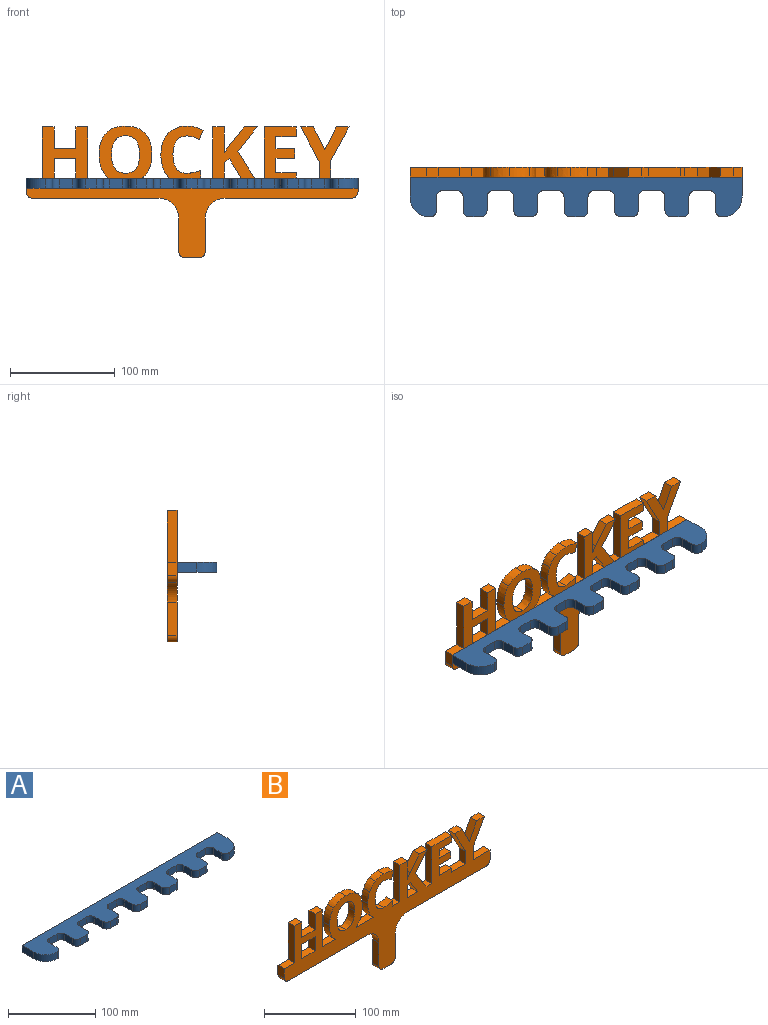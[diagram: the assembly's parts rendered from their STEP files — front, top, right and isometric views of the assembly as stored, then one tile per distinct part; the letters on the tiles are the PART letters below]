
ASSEMBLY  parts=2 mates=1
PART A: 54 faces, bbox 317.5x38.1x9.5 mm
  f0: cylinder r=6.35mm len=9.53mm, axis (0,0,-1), area 95mm2, adj f1,f51,f52,f53
  f1: plane 12.7x9.53mm, normal (0,-1,0), area 121mm2, adj f0,f2,f52,f53
  f2: cylinder r=6.35mm len=9.53mm, axis (0,0,-1), area 95mm2, adj f1,f3,f52,f53
  f3: plane 12.7x9.53mm, normal (-1,0,0), area 121mm2, adj f2,f4,f52,f53
  f4: cylinder r=6.35mm len=9.53mm, axis (0,0,-1), area 95mm2, adj f3,f5,f52,f53
  f5: plane 10.16x9.53mm, normal (0,-1,0), area 96.8mm2, adj f4,f6,f52,f53
  f6: cylinder r=6.35mm len=9.53mm, axis (0,0,-1), area 95mm2, adj f5,f7,f52,f53
  f7: plane 12.7x9.53mm, normal (1,0,0), area 121mm2, adj f6,f8,f52,f53
  f8: cylinder r=6.35mm len=9.53mm, axis (0,0,-1), area 95mm2, adj f7,f9,f52,f53
  f9: plane 12.7x9.53mm, normal (0,-1,0), area 121mm2, adj f8,f10,f52,f53
  f10: cylinder r=6.35mm len=9.53mm, axis (0,0,-1), area 95mm2, adj f9,f11,f52,f53
  f11: plane 12.7x9.53mm, normal (-1,0,0), area 121mm2, adj f10,f12,f52,f53
  f12: cylinder r=6.35mm len=9.53mm, axis (0,0,-1), area 95mm2, adj f11,f13,f52,f53
  f13: plane 10.16x9.53mm, normal (0,-1,0), area 96.8mm2, adj f12,f14,f52,f53
  f14: cylinder r=6.35mm len=9.53mm, axis (0,0,-1), area 95mm2, adj f13,f15,f52,f53
  f15: plane 12.7x9.53mm, normal (1,0,0), area 121mm2, adj f14,f16,f52,f53
  f16: cylinder r=6.35mm len=9.53mm, axis (0,0,-1), area 95mm2, adj f15,f17,f52,f53
  f17: plane 12.7x9.53mm, normal (0,-1,0), area 121mm2, adj f16,f18,f52,f53
  f18: cylinder r=6.35mm len=9.53mm, axis (0,0,-1), area 95mm2, adj f17,f19,f52,f53
  f19: plane 12.7x9.53mm, normal (-1,0,0), area 121mm2, adj f18,f20,f52,f53
  f20: cylinder r=6.35mm len=9.53mm, axis (0,0,-1), area 95mm2, adj f19,f21,f52,f53
  f21: plane 10.16x9.53mm, normal (0,-1,0), area 96.8mm2, adj f20,f22,f52,f53
  f22: cylinder r=6.35mm len=9.53mm, axis (0,0,-1), area 95mm2, adj f21,f23,f52,f53
  f23: plane 12.7x9.53mm, normal (1,0,0), area 121mm2, adj f22,f24,f52,f53
  f24: cylinder r=6.35mm len=9.53mm, axis (0,0,-1), area 95mm2, adj f23,f25,f52,f53
  f25: plane 12.7x9.53mm, normal (0,-1,0), area 121mm2, adj f24,f26,f52,f53
  f26: cylinder r=6.35mm len=9.53mm, axis (0,0,-1), area 95mm2, adj f25,f27,f52,f53
  f27: plane 12.7x9.53mm, normal (-1,0,0), area 121mm2, adj f26,f28,f52,f53
  f28: cylinder r=6.35mm len=9.53mm, axis (0,0,-1), area 95mm2, adj f27,f29,f52,f53
  f29: plane 10.16x9.53mm, normal (0,-1,0), area 96.8mm2, adj f28,f30,f52,f53
  f30: cylinder r=6.35mm len=9.53mm, axis (0,0,-1), area 95mm2, adj f29,f31,f52,f53
  f31: plane 12.7x9.53mm, normal (1,0,0), area 121mm2, adj f30,f32,f52,f53
  f32: cylinder r=6.35mm len=9.53mm, axis (0,0,-1), area 95mm2, adj f31,f33,f52,f53
  f33: plane 12.7x9.53mm, normal (0,-1,0), area 121mm2, adj f32,f34,f52,f53
  f34: cylinder r=6.35mm len=9.53mm, axis (0,0,-1), area 95mm2, adj f33,f35,f52,f53
  f35: plane 12.7x9.53mm, normal (-1,0,0), area 121mm2, adj f34,f36,f52,f53
  f36: cylinder r=6.35mm len=9.53mm, axis (0,0,-1), area 95mm2, adj f35,f37,f52,f53
  f37: plane 10.16x9.53mm, normal (0,-1,0), area 96.8mm2, adj f36,f38,f52,f53
  f38: cylinder r=6.35mm len=9.53mm, axis (0,0,-1), area 95mm2, adj f37,f39,f52,f53
  f39: plane 12.7x9.53mm, normal (1,0,0), area 121mm2, adj f38,f40,f52,f53
  f40: cylinder r=6.35mm len=9.53mm, axis (0,0,-1), area 95mm2, adj f39,f41,f52,f53
  f41: plane 12.7x9.53mm, normal (0,-1,0), area 121mm2, adj f40,f42,f52,f53
  f42: cylinder r=6.35mm len=9.53mm, axis (0,0,-1), area 95mm2, adj f41,f43,f52,f53
  f43: plane 12.7x9.53mm, normal (-1,0,0), area 121mm2, adj f42,f44,f52,f53
  f44: cylinder r=6.35mm len=9.53mm, axis (0,0,-1), area 95mm2, adj f43,f45,f52,f53
  f45: cylinder r=19.05mm len=19.05mm, axis (0,0,-1), area 285mm2, adj f44,f46,f52,f53
  f46: plane 19.05x9.53mm, normal (1,0,0), area 181.5mm2, adj f45,f47,f52,f53
  f47: plane 317.5x9.53mm, normal (0,1,0), area 3024.2mm2, adj f46,f48,f52,f53
  f48: plane 19.05x9.53mm, normal (-1,0,0), area 181.5mm2, adj f47,f49,f52,f53
  f49: cylinder r=19.05mm len=19.05mm, axis (0,0,-1), area 285mm2, adj f48,f50,f52,f53
  f50: cylinder r=6.35mm len=9.53mm, axis (0,0,-1), area 95mm2, adj f49,f51,f52,f53
  f51: plane 12.7x9.53mm, normal (1,0,0), area 121mm2, adj f0,f50,f52,f53
  f52: plane 317.5x38.1mm, normal (0,0,1), area 8070mm2, adj f0,f1,f2,f3,f4,f5,f6,f7
  f53: plane 317.5x38.1mm, normal (0,0,-1), area 8070mm2, adj f0,f1,f2,f3,f4,f5,f6,f7
PART B: 92 faces, bbox 317.5x9.5x126.2 mm
  f0: plane 20.96x9.53mm, normal (0,0,1), area 199.6mm2, adj f1,f89,f90,f91
  f1: plane 19.03x9.53mm, normal (1,0,0), area 181.3mm2, adj f0,f2,f90,f91
  f2: plane 20.96x9.53mm, normal (0,0,-1), area 199.6mm2, adj f1,f89,f90,f91
  f3: plane 18.49x11.5mm, normal (-0.85,0,-0.53), area 207.4mm2, adj f4,f86,f90,f91
  f4: plane 16.24x9.53mm, normal (0,0,1), area 154.6mm2, adj f3,f5,f90,f91
  f5: plane 15.08x9.53mm, normal (1,0,0), area 143.7mm2, adj f4,f86,f90,f91
  f6: extruded ~13.36x9.53mm, area 133.5mm2, adj f7,f87,f90,f91
  f7: extruded ~13.37x9.53mm, area 133.6mm2, adj f6,f8,f90,f91
  f8: extruded ~10.1x9.53mm, area 109.5mm2, adj f7,f9,f90,f91
  f9: extruded ~17.87x13.36mm, area 242.4mm2, adj f8,f10,f90,f91
  f10: extruded ~17.85x13.43mm, area 242.7mm2, adj f9,f87,f90,f91
  f11: plane 49.12x9.53mm, normal (-1,0,0), area 467.8mm2, adj f12,f88,f90,f91
  f12: plane 9.53x9.06mm, normal (0,0,1), area 86.3mm2, adj f11,f13,f90,f91
  f13: plane 25.69x16.2mm, normal (0.85,0,0.53), area 289.3mm2, adj f12,f14,f90,f91
  f14: plane 23.42x18.47mm, normal (0.79,0,-0.62), area 284.1mm2, adj f13,f15,f90,f91
  f15: plane 12.45x9.53mm, normal (0,0,1), area 118.6mm2, adj f14,f16,f90,f91
  f16: plane 17.99x14.34mm, normal (-0.78,0,0.62), area 219.1mm2, adj f15,f17,f90,f91
  f17: plane 9.53x6.23mm, normal (-0.82,0,0.58), area 72.7mm2, adj f16,f18,f90,f91
  f18: plane 24.22x9.53mm, normal (1,0,0), area 230.7mm2, adj f17,f19,f90,f91
  f19: plane 11.23x9.53mm, normal (0,0,1), area 106.9mm2, adj f18,f20,f90,f91
  f20: plane 49.12x9.53mm, normal (-1,0,0), area 467.8mm2, adj f19,f21,f90,f91
  f21: plane 11.26x9.53mm, normal (0,0,1), area 107.2mm2, adj f20,f22,f90,f91
  f22: plane 9.53x7.59mm, normal (1,0,0), area 72.3mm2, adj f21,f23,f90,f91
  f23: extruded ~13.5x9.53mm, area 131.8mm2, adj f22,f24,f90,f91
  f24: extruded ~17.7x13.29mm, area 240.5mm2, adj f23,f25,f90,f91
  f25: extruded ~13.26x9.53mm, area 132.8mm2, adj f24,f26,f90,f91
  f26: extruded ~9.81x9.53mm, area 108.2mm2, adj f25,f27,f90,f91
  f27: extruded ~9.53x5.9mm, area 57.3mm2, adj f26,f28,f90,f91
  f28: extruded ~9.53x5.98mm, area 61.6mm2, adj f27,f29,f90,f91
  f29: plane 9.53x9.13mm, normal (0.93,0,-0.37), area 93.5mm2, adj f28,f30,f90,f91
  f30: extruded ~15.49x9.53mm, area 153mm2, adj f29,f31,f90,f91
  f31: extruded ~13.19x9.53mm, area 131.1mm2, adj f30,f32,f90,f91
  f32: extruded ~9.53x9.52mm, area 124.3mm2, adj f31,f33,f90,f91
  f33: extruded ~14.47x9.53mm, area 142mm2, adj f32,f34,f90,f91
  f34: extruded ~20.11x9.53mm, area 204.6mm2, adj f33,f35,f90,f91
  f35: extruded ~9.53x2.59mm, area 34.2mm2, adj f34,f36,f90,f91
  f36: plane 26.65x9.53mm, normal (0,0,1), area 253.8mm2, adj f35,f37,f90,f91
  f37: extruded ~9.53x2.8mm, area 36mm2, adj f36,f38,f90,f91
  f38: extruded ~20.21x9.53mm, area 207.1mm2, adj f37,f39,f90,f91
  f39: extruded ~20.2x9.53mm, area 206.8mm2, adj f38,f40,f90,f91
  f40: extruded ~18.66x9.53mm, area 195.7mm2, adj f39,f41,f90,f91
  f41: extruded ~18.73x9.53mm, area 196mm2, adj f40,f42,f90,f91
  f42: extruded ~20.19x9.53mm, area 207mm2, adj f41,f43,f90,f91
  f43: extruded ~20.28x9.53mm, area 207.7mm2, adj f42,f44,f90,f91
  f44: extruded ~9.53x2.8mm, area 36mm2, adj f43,f45,f90,f91
  f45: plane 20.32x9.53mm, normal (0,0,1), area 193.6mm2, adj f44,f46,f90,f91
  f46: plane 49.12x9.53mm, normal (1,0,0), area 467.8mm2, adj f45,f47,f90,f91
  f47: plane 11.19x9.53mm, normal (0,0,1), area 106.6mm2, adj f46,f48,f90,f91
  f48: plane 20.75x9.53mm, normal (-1,0,0), area 197.6mm2, adj f47,f49,f90,f91
  f49: plane 20.96x9.53mm, normal (0,0,1), area 199.6mm2, adj f48,f50,f90,f91
  f50: plane 20.75x9.53mm, normal (1,0,0), area 197.6mm2, adj f49,f51,f90,f91
  f51: plane 11.23x9.53mm, normal (0,0,1), area 106.9mm2, adj f50,f52,f90,f91
  f52: plane 49.12x9.53mm, normal (-1,0,0), area 467.8mm2, adj f51,f53,f90,f91
  f53: plane 15.61x9.53mm, normal (0,0,1), area 148.7mm2, adj f52,f54,f90,f91
  f54: plane 12.7x9.53mm, normal (-1,0,0), area 121mm2, adj f53,f55,f90,f91
  f55: cylinder r=6.35mm len=9.53mm, axis (0,1,0), area 95mm2, adj f54,f56,f90,f91
  f56: plane 120.65x9.53mm, normal (0,0,-1), area 1149.2mm2, adj f55,f57,f90,f91
  f57: cylinder r=19.05mm len=19.05mm, axis (0,1,0), area 285mm2, adj f56,f58,f90,f91
  f58: plane 31.75x9.53mm, normal (-1,0,0), area 302.4mm2, adj f57,f59,f90,f91
  f59: cylinder r=6.35mm len=9.53mm, axis (0,1,0), area 95mm2, adj f58,f60,f90,f91
  f60: plane 12.7x9.53mm, normal (0,0,-1), area 121mm2, adj f59,f61,f90,f91
  f61: cylinder r=6.35mm len=9.53mm, axis (0,1,0), area 95mm2, adj f60,f62,f90,f91
  f62: plane 31.75x9.53mm, normal (1,0,0), area 302.4mm2, adj f61,f63,f90,f91
  f63: cylinder r=19.05mm len=19.05mm, axis (0,1,0), area 285mm2, adj f62,f64,f90,f91
  f64: plane 120.65x9.53mm, normal (0,0,-1), area 1149.2mm2, adj f63,f65,f90,f91
  f65: cylinder r=6.35mm len=9.53mm, axis (0,1,0), area 95mm2, adj f64,f66,f90,f91
  f66: plane 12.7x9.53mm, normal (1,0,0), area 121mm2, adj f65,f67,f90,f91
  f67: plane 26.12x9.53mm, normal (0,0,1), area 248.8mm2, adj f66,f68,f90,f91
  f68: plane 16.79x9.53mm, normal (1,0,0), area 159.9mm2, adj f67,f69,f90,f91
  f69: plane 32.33x17.56mm, normal (0.88,0,-0.48), area 350.5mm2, adj f68,f70,f90,f91
  f70: plane 12.09x9.53mm, normal (0,0,1), area 115.2mm2, adj f69,f71,f90,f91
  f71: plane 21.79x11.04mm, normal (-0.89,0,0.45), area 232.7mm2, adj f70,f72,f90,f91
  f72: plane 21.79x10.97mm, normal (0.89,0,0.45), area 232.4mm2, adj f71,f73,f90,f91
  f73: plane 12.16x9.53mm, normal (0,0,1), area 115.9mm2, adj f72,f74,f90,f91
  f74: plane 32.69x17.56mm, normal (-0.88,0,-0.47), area 353.5mm2, adj f73,f75,f90,f91
  f75: plane 16.43x9.53mm, normal (-1,0,0), area 156.5mm2, adj f74,f76,f90,f91
  f76: plane 21.94x9.53mm, normal (0,0,1), area 209mm2, adj f75,f77,f90,f91
  f77: plane 9.53x5.46mm, normal (1,0,0), area 52mm2, adj f76,f78,f90,f91
  f78: plane 19.25x9.53mm, normal (0,0,1), area 183.4mm2, adj f77,f79,f90,f91
  f79: plane 13.65x9.53mm, normal (1,0,0), area 130mm2, adj f78,f80,f90,f91
  f80: plane 17.92x9.53mm, normal (0,0,-1), area 170.7mm2, adj f79,f81,f90,f91
  f81: plane 9.53x9.2mm, normal (1,0,0), area 87.6mm2, adj f80,f82,f90,f91
  f82: plane 17.92x9.53mm, normal (0,0,1), area 170.7mm2, adj f81,f83,f90,f91
  f83: plane 11.62x9.53mm, normal (1,0,0), area 110.7mm2, adj f82,f84,f90,f91
  f84: plane 19.25x9.53mm, normal (0,0,-1), area 183.4mm2, adj f83,f85,f90,f91
  f85: plane 9.53x9.2mm, normal (1,0,0), area 87.6mm2, adj f84,f88,f90,f91
  f86: plane 9.53x4.74mm, normal (0.58,0,-0.81), area 55.6mm2, adj f3,f5,f90,f91
  f87: extruded ~10.06x9.53mm, area 109.1mm2, adj f6,f10,f90,f91
  f88: plane 30.48x9.53mm, normal (0,0,1), area 290.3mm2, adj f11,f85,f90,f91
  f89: plane 19.03x9.53mm, normal (-1,0,0), area 181.3mm2, adj f0,f2,f90,f91
  f90: plane 317.5x126.15mm, normal (0,-1,0), area 14235.5mm2, adj f0,f1,f2,f3,f4,f5,f6,f7
  f91: plane 317.5x126.15mm, normal (0,1,0), area 14235.5mm2, adj f0,f1,f2,f3,f4,f5,f6,f7
PLACE A t=(17.66,-13.08,13.93)mm
PLACE B t=(17.66,9.15,-14.65)mm
MATE fastened B.f90 <-> A.f47  axis (0,-1,0) through (176.41,-0.38,23.45)mm
